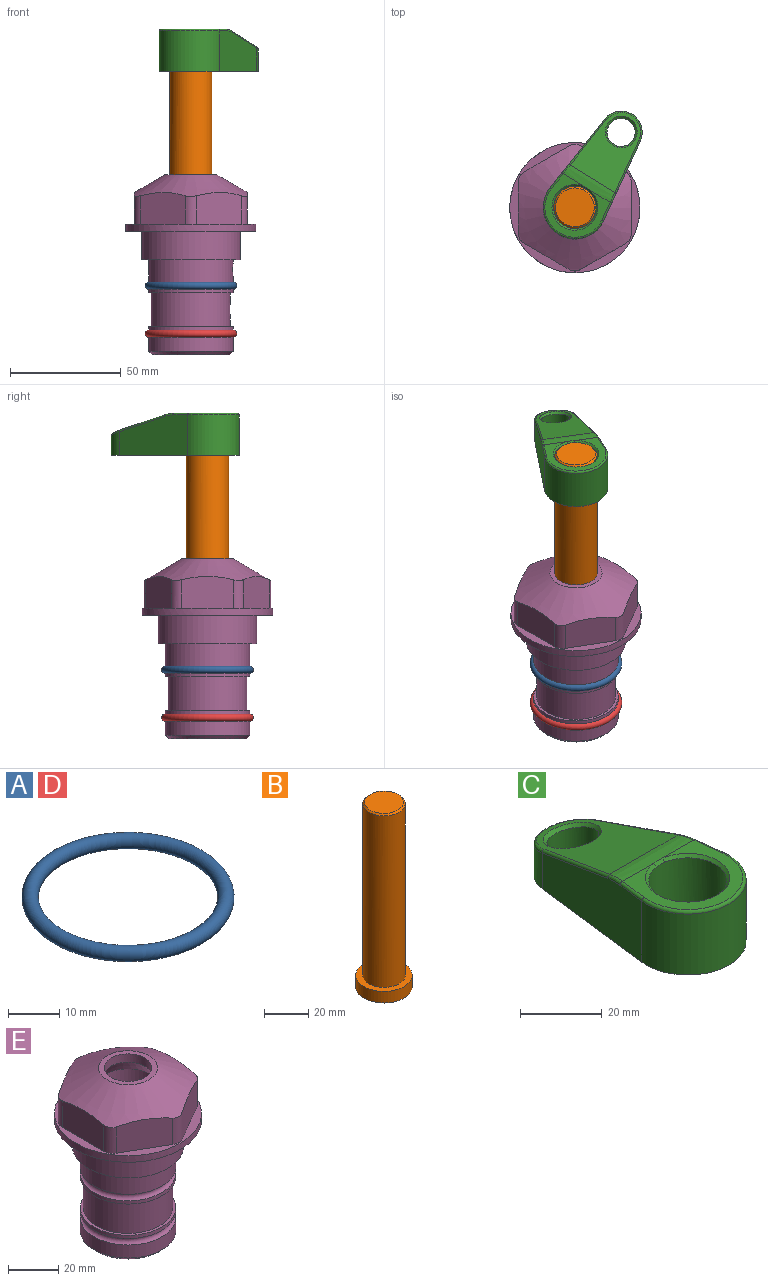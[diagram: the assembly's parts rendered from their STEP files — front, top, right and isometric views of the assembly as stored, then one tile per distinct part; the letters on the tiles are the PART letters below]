
ASSEMBLY  parts=5 mates=4
PART A: 1 faces, bbox 44.7x44.7x3.2 mm
  f0: torus R=19.05mm, axis (0,0,1), area 1193.9mm2
PART B: 6 faces, bbox 25.4x25.4x101.6 mm
  f0: plane 17.46x17.46mm, normal (0,0,1), area 239.5mm2, adj f5
  f1: plane 25.4x25.4mm, normal (0,0,-1), area 506.7mm2, adj f2
  f2: cylinder r=12.7mm len=25.4mm, axis (0,0,1), area 506.7mm2, adj f1,f3
  f3: plane 25.4x25.4mm, normal (0,0,1), area 221.7mm2, adj f2,f4
  f4: cylinder r=9.53mm len=94.46mm, axis (0,0,1), area 5653mm2, adj f3,f5
  f5: cone r=8.73mm half-angle=45deg, axis (0,0,-1), area 64.4mm2, adj f0,f4
PART C: 31 faces, bbox 31.7x65.5x19.8 mm
  f0: plane 39.12x18.26mm, normal (0.99,0.12,0), area 612.2mm2, adj f1,f4,f7,f11,f13,f15
  f1: cylinder r=9.53mm len=18.91mm, axis (0,0,-1), area 296.1mm2, adj f0,f2,f7,f17
  f2: plane 39.12x18.26mm, normal (-0.99,0.12,0), area 612.2mm2, adj f1,f4,f7,f12,f14,f16
  f3: cylinder r=6.35mm len=12.7mm, axis (0,0,-1), area 362.4mm2, adj f7,f18
  f4: cylinder r=14.29mm len=28.58mm, axis (0,0,-1), area 882.2mm2, adj f0,f2,f7,f10
  f5: cylinder r=9.53mm len=19.05mm, axis (0,0,-1), area 1092.6mm2, adj f7,f19,f20
  f6: plane 26.99x23.69mm, normal (0,0,1), area 216.2mm2, adj f9,f10,f11,f12,f19
  f7: plane 63.5x28.58mm, normal (0,0,-1), area 661.8mm2, adj f0,f1,f2,f3,f4,f5,f22,f23
  f8: plane 33.52x23.6mm, normal (0,0.26,0.97), area 486mm2, adj f9,f15,f16,f17,f18
  f9: cylinder r=19.05mm len=24.72mm, axis (1,0,0), area 120.4mm2, adj f6,f8,f13,f14,f20
  f10: torus R=13.49mm, axis (0,0,1), area 59mm2, adj f4,f6,f11,f12
  f11: cylinder r=0.79mm len=8.67mm, axis (0.12,-0.99,0), area 10.8mm2, adj f0,f6,f10,f13
  f12: cylinder r=0.79mm len=8.67mm, axis (0.12,0.99,0), area 10.8mm2, adj f2,f6,f10,f14
  f13: bspline ~4.95x1.42mm, area 6.1mm2, adj f0,f9,f11,f15
  f14: bspline ~4.95x1.42mm, area 6.1mm2, adj f2,f9,f12,f16
  f15: cylinder r=0.79mm len=25.95mm, axis (0.12,-0.96,0.26), area 32.9mm2, adj f0,f8,f13,f17
  f16: cylinder r=0.79mm len=25.95mm, axis (0.12,0.96,-0.26), area 32.9mm2, adj f2,f8,f14,f17
  f17: bspline ~18.91x8.38mm, area 30mm2, adj f1,f8,f15,f16
  f18: bspline ~14.29x14.29mm, area 48.3mm2, adj f3,f8
  f19: cone r=9.53mm half-angle=45deg, axis (0,0,1), area 66.5mm2, adj f5,f6,f20
  f20: bspline ~3.22x0.96mm, area 3.5mm2, adj f5,f9,f19
  f21: plane 2.75x2.72mm, normal (0,0,-1), area 2.9mm2, adj f23,f25,f28
  f22: plane 23.05x15.88mm, normal (-0.99,-0.12,0), area 323.6mm2, adj f7,f25,f26,f27,f28,f29
  f23: plane 23.05x15.88mm, normal (0.99,-0.12,0), area 323.6mm2, adj f7,f21,f25,f27,f28,f30
  f24: cylinder r=9.53mm len=10.69mm, axis (0,0,-1), area 114.7mm2, adj f7,f27,f29,f30
  f25: cylinder r=12.7mm len=20.59mm, axis (0,0,-1), area 381.1mm2, adj f7,f21,f22,f23,f26,f28
  f26: plane 2.75x2.72mm, normal (0,0,-1), area 2.9mm2, adj f22,f25,f28
  f27: plane 19.72x18.37mm, normal (0,-0.26,-0.97), area 291.8mm2, adj f22,f23,f24,f28,f29,f30
  f28: cylinder r=15.88mm len=19.92mm, axis (1,0,0), area 54.8mm2, adj f21,f22,f23,f25,f26,f27
  f29: cylinder r=1.59mm len=11mm, axis (0,0,-1), area 34.7mm2, adj f7,f22,f24,f27
  f30: cylinder r=1.59mm len=11mm, axis (0,0,-1), area 34.7mm2, adj f7,f23,f24,f27
PART D: same geometry as A
PART E: 36 faces, bbox 58.7x58.7x81 mm
  f0: cylinder r=17.78mm len=35.56mm, axis (0,0,1), area 1670.8mm2, adj f23,f24,f31
  f1: cylinder r=19.05mm len=38.1mm, axis (0,0,1), area 1191.9mm2, adj f26,f27,f30
  f2: plane 58.66x58.66mm, normal (0,0,-1), area 1150.6mm2, adj f3,f28
  f3: cylinder r=29.33mm len=58.66mm, axis (0,0,-1), area 585.1mm2, adj f2,f4
  f4: plane 58.66x58.66mm, normal (0,0,1), area 475.9mm2, adj f3,f5,f6,f7,f8,f9,f10,f11
  f5: plane 20.32x14.34mm, normal (-0.5,0.87,0), area 324.4mm2, adj f4,f15,f16,f17
  f6: plane 20.32x14.34mm, normal (0.5,0.87,0), area 324.4mm2, adj f4,f14,f15,f17
  f7: plane 23.48x14.34mm, normal (1,0,0), area 324.4mm2, adj f4,f13,f14,f17
  f8: plane 20.32x14.34mm, normal (0.5,-0.87,0), area 324.4mm2, adj f4,f12,f13,f17
  f9: plane 20.32x14.34mm, normal (-0.5,-0.87,0), area 324.4mm2, adj f4,f11,f12,f17
  f10: plane 23.48x14.34mm, normal (-1,0,0), area 324.4mm2, adj f4,f11,f16,f17
  f11: cylinder r=5.08mm len=12.85mm, axis (0,0,-1), area 67.2mm2, adj f4,f9,f10,f17
  f12: cylinder r=5.08mm len=12.85mm, axis (0,0,-1), area 67.2mm2, adj f4,f8,f9,f17
  f13: cylinder r=5.08mm len=12.85mm, axis (0,0,-1), area 67.2mm2, adj f4,f7,f8,f17
  f14: cylinder r=5.08mm len=12.85mm, axis (0,0,-1), area 67.2mm2, adj f4,f6,f7,f17
  f15: cylinder r=5.08mm len=12.85mm, axis (0,0,-1), area 67.2mm2, adj f4,f5,f6,f17
  f16: cylinder r=5.08mm len=12.85mm, axis (0,0,-1), area 67.2mm2, adj f4,f5,f10,f17
  f17: cone r=11.73mm half-angle=60deg, axis (0,0,-1), area 2071.8mm2, adj f5,f6,f7,f8,f9,f10,f11,f12
  f18: plane 23.46x23.46mm, normal (0,0,1), area 147.4mm2, adj f17,f35
  f19: plane 34.93x34.93mm, normal (0,0,-1), area 958mm2, adj f29
  f20: cylinder r=19.05mm len=38.1mm, axis (0,0,1), area 760.1mm2, adj f21,f29
  f21: torus R=19.05mm, axis (0,0,1), area 565.3mm2, adj f20,f22
  f22: cylinder r=19.05mm len=38.1mm, axis (0,0,1), area 190mm2, adj f21,f23
  f23: plane 38.1x38.1mm, normal (0,0,1), area 146.9mm2, adj f0,f22
  f24: plane 38.1x38.1mm, normal (0,0,-1), area 146.9mm2, adj f0,f25
  f25: cylinder r=19.05mm len=38.1mm, axis (0,0,1), area 190mm2, adj f24,f26
  f26: torus R=19.05mm, axis (0,0,1), area 565.3mm2, adj f1,f25
  f27: plane 44.45x44.45mm, normal (0,0,-1), area 411.7mm2, adj f1,f28
  f28: cylinder r=22.23mm len=44.45mm, axis (0,0,1), area 1773.5mm2, adj f2,f27
  f29: cone r=19.05mm half-angle=45deg, axis (0,0,1), area 257.5mm2, adj f19,f20
  f30: cylinder r=3.17mm len=6.75mm, axis (-1,0,0), area 128mm2, adj f1,f33
  f31: cylinder r=3.17mm len=6.35mm, axis (-1,0,0), area 102.5mm2, adj f0,f33
  f32: plane 25.4x25.4mm, normal (0,0,1), area 506.7mm2, adj f33
  f33: cylinder r=12.7mm len=66.42mm, axis (0,0,-1), area 5236.2mm2, adj f30,f31,f32,f34
  f34: cone r=9.53mm half-angle=30deg, axis (0,0,-1), area 443.4mm2, adj f33,f35
  f35: cylinder r=9.53mm len=19.05mm, axis (0,0,-1), area 240.9mm2, adj f18,f34
PLACE A at identity
PLACE B rot(axis=(0,0,-1),31.6deg) t=(0,0,27.55)mm
PLACE C rot(axis=(0,0,-1),31.6deg) t=(0,0,27.55)mm
PLACE D t=(0,0,-21.59)mm
PLACE E at identity fixed
MATE cylindrical B.f2 <-> E.f0  axis (0,0,-1) through (0,0,-10.55)mm
MATE fastened A.f0 <-> E.f0  axis (0,0,1) through (0,0,-24.51)mm
MATE fastened D.f0 <-> E.f0  axis (0,0,1) through (0,0,-46.1)mm
MATE fastened C.f4 <-> B.f2  axis (0,0,1) through (0,0,91.05)mm
